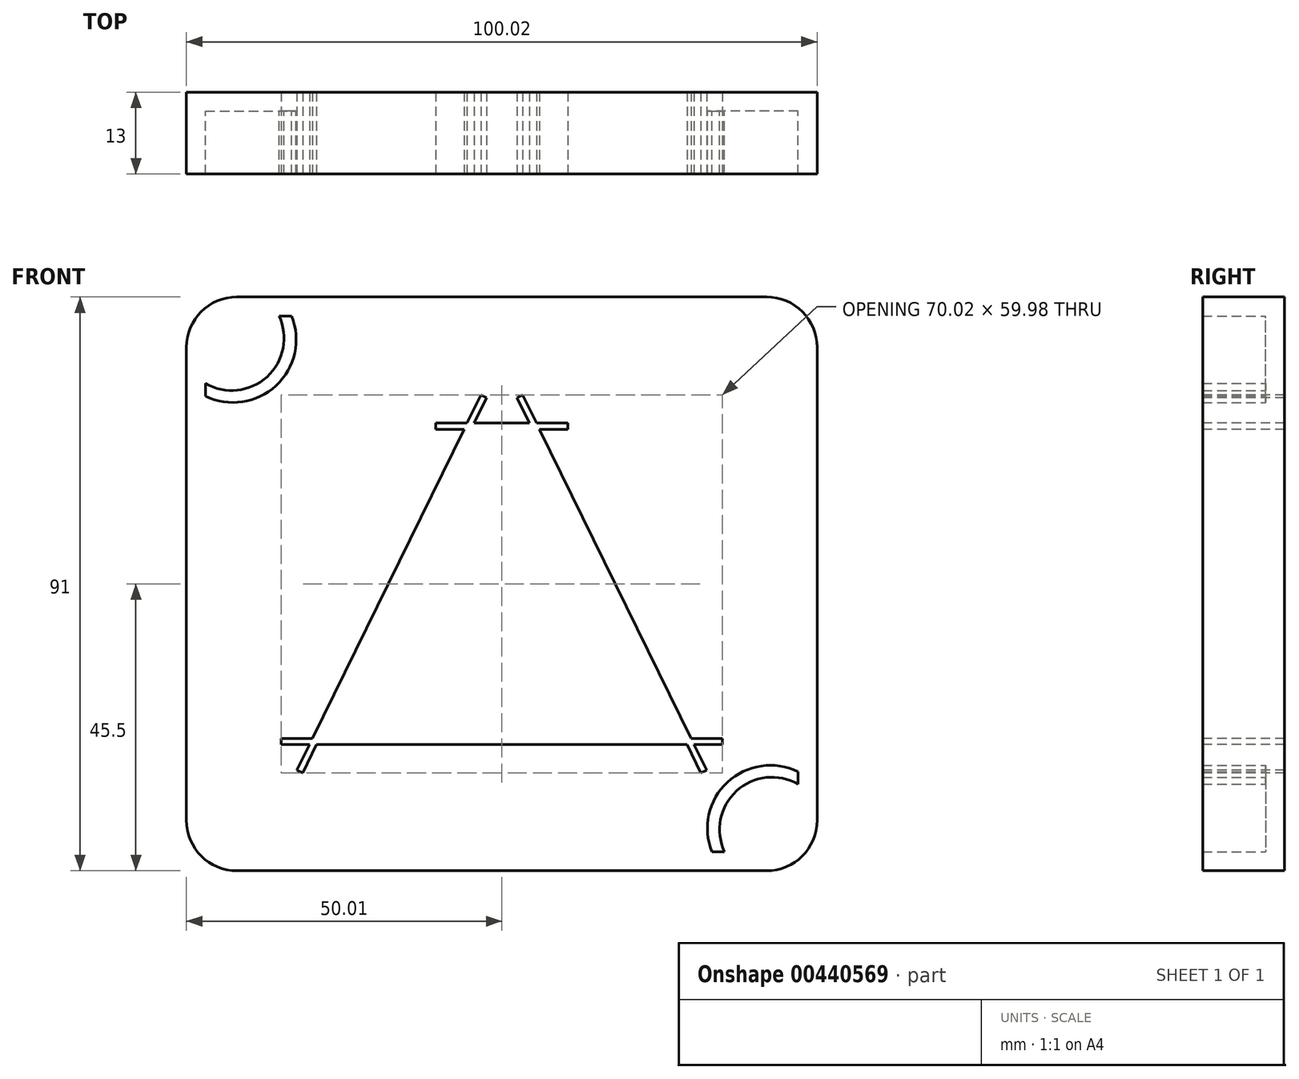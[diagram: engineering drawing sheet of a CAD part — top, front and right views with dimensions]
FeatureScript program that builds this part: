
annotation { "Feature Type Name" : "Feature", "Feature Type Description" : "" }
export const myFeature = defineFeature(function(context is Context, id is Id, definition is map)
    precondition{}
    {
        {
            var Q0;
            Q0=qCreatedBy(makeId("Front.planeOp"),FACE);
            var sketch = newSketch(context, id + "F0", { "sketchPlane" : qUnion([Q0])});
            skLineSegment(sketch, "E0", {"start": v(-29.39, 0) * mm, "end": v(0, 0) * mm});
            skLineSegment(sketch, "E1", {"start": v(0, 51) * mm, "end": v(-4.39, 51) * mm});
            skLineSegment(sketch, "E2", {"start": v(-6, 50) * mm, "end": v(-30, 1) * mm});
            skLineSegment(sketch, "E3", {"start": v(-31.61, 0) * mm, "end": v(-35, 0) * mm});
            skLineSegment(sketch, "E4", {"start": v(-35, 0) * mm, "end": v(-35, 1) * mm});
            skLineSegment(sketch, "E5", {"start": v(-35, 1) * mm, "end": v(-30, 1) * mm});
            skLineSegment(sketch, "E6", {"start": v(-5.5, 51) * mm, "end": v(-10.5, 51) * mm});
            skLineSegment(sketch, "E7", {"start": v(-5, 52) * mm, "end": v(-3.3, 55.49) * mm});
            skLineSegment(sketch, "E8.trimOffspring", {"start": v(-30.5, 0) * mm, "end": v(-32.49, -4.05) * mm});
            skPoint(sketch, "E9.end.orphan", {"position": v(-5.5, 55.49) * mm});
            skPoint(sketch, "E10.end.orphan", {"position": v(-7.96, 50.47) * mm});
            skPoint(sketch, "E11.trimOffspring.end.orphan", {"position": v(-5.5, 50.47) * mm});
            skLineSegment(sketch, "E12", {"start": v(-3.3, 55.49) * mm, "end": v(-2.4, 55.05) * mm});
            skLineSegment(sketch, "E13", {"start": v(-2.4, 55.05) * mm, "end": v(-4.39, 51) * mm});
            skPoint(sketch, "E14.end.orphan", {"position": v(6.46, 54.86) * mm});
            skPoint(sketch, "E15.end.orphan", {"position": v(5.5, 56.81) * mm});
            skPoint(sketch, "E16.end.orphan", {"position": v(13.73, 54.86) * mm});
            skLineSegment(sketch, "E17", {"start": v(-10.5, 51) * mm, "end": v(-10.5, 50) * mm});
            skLineSegment(sketch, "E18", {"start": v(-10.5, 50) * mm, "end": v(-6, 50) * mm});
            skLineSegment(sketch, "E19", {"start": v(-5, 52) * mm, "end": v(-5.5, 51) * mm});
            skLineSegment(sketch, "E20", {"start": v(-32.49, -4.05) * mm, "end": v(-31.59, -4.49) * mm});
            skLineSegment(sketch, "E21", {"start": v(-31.59, -4.49) * mm, "end": v(-29.39, 0) * mm});
            skLineSegment(sketch, "E22", {"start": v(-31.61, 0) * mm, "end": v(-30.5, 0) * mm});
            skLineSegment(sketch, "E23", {"start": v(0, 61.62) * mm, "end": v(0, -9.78) * mm, "construction": true});
            skPoint(sketch, "E24.start.orphan", {"position": v(5.5, 51) * mm});
            skLineSegment(sketch, "E25.MirrorCS", {"start": v(5, 52) * mm, "end": v(5.5, 51) * mm});
            skLineSegment(sketch, "E26.MirrorCS", {"start": v(31.61, 0) * mm, "end": v(30.5, 0) * mm});
            skLineSegment(sketch, "E27.MirrorCS", {"start": v(10.5, 51) * mm, "end": v(10.5, 50) * mm});
            skLineSegment(sketch, "E28.MirrorCS", {"start": v(31.61, 0) * mm, "end": v(35, 0) * mm});
            skLineSegment(sketch, "E29.MirrorCS", {"start": v(32.49, -4.05) * mm, "end": v(31.59, -4.49) * mm});
            skLineSegment(sketch, "E30.MirrorCS", {"start": v(2.4, 55.05) * mm, "end": v(4.39, 51) * mm});
            skLineSegment(sketch, "E31.MirrorCS", {"start": v(3.3, 55.49) * mm, "end": v(2.4, 55.05) * mm});
            skLineSegment(sketch, "E32.MirrorCS", {"start": v(30.5, 0) * mm, "end": v(32.49, -4.05) * mm});
            skLineSegment(sketch, "E33.MirrorCS", {"start": v(5, 52) * mm, "end": v(3.3, 55.49) * mm});
            skLineSegment(sketch, "E34.MirrorCS", {"start": v(35, 1) * mm, "end": v(30, 1) * mm});
            skLineSegment(sketch, "E35.MirrorCS", {"start": v(35, 0) * mm, "end": v(35, 1) * mm});
            skLineSegment(sketch, "E36.MirrorCS", {"start": v(10.5, 50) * mm, "end": v(6, 50) * mm});
            skLineSegment(sketch, "E37.MirrorCS", {"start": v(0, 51) * mm, "end": v(4.39, 51) * mm});
            skLineSegment(sketch, "E38.MirrorCS", {"start": v(31.59, -4.49) * mm, "end": v(29.39, 0) * mm});
            skLineSegment(sketch, "E39.MirrorCS", {"start": v(5.5, 51) * mm, "end": v(10.5, 51) * mm});
            skLineSegment(sketch, "E40.MirrorCS", {"start": v(6, 50) * mm, "end": v(30, 1) * mm});
            skPoint(sketch, "E41.MirrorP", {"position": v(5.5, 50.47) * mm});
            skPoint(sketch, "E42.MirrorP", {"position": v(5.5, 55.49) * mm});
            skPoint(sketch, "E43.MirrorP", {"position": v(7.96, 50.47) * mm});
            skLineSegment(sketch, "E44.MirrorCS", {"start": v(29.39, 0) * mm, "end": v(0, 0) * mm});
            skLineSegment(sketch, "E45.bottom", {"start": v(-50, 71) * mm, "end": v(50, 71) * mm});
            skLineSegment(sketch, "E45.top", {"start": v(-50, -20) * mm, "end": v(50, -20) * mm});
            skLineSegment(sketch, "E45.left", {"start": v(-50, 71) * mm, "end": v(-50, -20) * mm});
            skLineSegment(sketch, "E45.right", {"start": v(50, 71) * mm, "end": v(50, -20) * mm});
            skPoint(sketch, "E45.middle", {"position": v(0, 25.5) * mm});
            skSolve(sketch);
        }
        {
            var Q0;
            Q0=makeQuery(id+"F0.imprint","IMPRINT",FACE,{"disambiguationData":[TD([[makeQuery(id+"F0.imprint","IMPRINT",EDGE,{"derivedFrom":sQuery(id+"F0.wireOp",EDGE,"E0")}),-1.0]])]});
            var sketch = newSketch(context, id + "F1", { "sketchPlane" : qUnion([Q0])});
            skArc(sketch, "E46", {"start": v(33.33, 68) * mm, "mid": v(35.8, 56.95) * mm, "end": v(47, 55.29) * mm});
            skLineSegment(sketch, "E47", {"start": v(50, 71) * mm, "end": v(-50, -20) * mm, "construction": true});
            skLineSegment(sketch, "E48", {"start": v(-50, 71) * mm, "end": v(50, -20) * mm, "construction": true});
            skLineSegment(sketch, "E49", {"start": v(-50, 25.5) * mm, "end": v(50, 25.5) * mm, "construction": true});
            skArc(sketch, "E50.MirrorCS", {"start": v(33.33, -17) * mm, "mid": v(35.8, -5.95) * mm, "end": v(47, -4.29) * mm});
            skArc(sketch, "E51.MirrorCS", {"start": v(-33.33, 68) * mm, "mid": v(-35.8, 56.95) * mm, "end": v(-47, 55.29) * mm});
            skArc(sketch, "E52.MirrorCS", {"start": v(-33.33, -17) * mm, "mid": v(-35.8, -5.95) * mm, "end": v(-47, -4.29) * mm});
            skLineSegment(sketch, "E53", {"start": v(33.33, 68) * mm, "end": v(35.33, 68) * mm});
            skLineSegment(sketch, "E54", {"start": v(47, 55.29) * mm, "end": v(47, 57.29) * mm});
            skArc(sketch, "E55", {"start": v(35.33, 68) * mm, "mid": v(37.23, 58.35) * mm, "end": v(47, 57.29) * mm});
            skArc(sketch, "E56.MirrorCS", {"start": v(-35.33, 68) * mm, "mid": v(-37.23, 58.35) * mm, "end": v(-47, 57.29) * mm});
            skLineSegment(sketch, "E57.MirrorCS", {"start": v(-33.33, 68) * mm, "end": v(-35.33, 68) * mm});
            skLineSegment(sketch, "E58.MirrorCS", {"start": v(-47, 55.29) * mm, "end": v(-47, 57.29) * mm});
            skLineSegment(sketch, "E59.MirrorCS", {"start": v(47, -4.29) * mm, "end": v(47, -6.29) * mm});
            skArc(sketch, "E60.MirrorCS", {"start": v(35.33, -17) * mm, "mid": v(37.23, -7.35) * mm, "end": v(47, -6.29) * mm});
            skLineSegment(sketch, "E61.MirrorCS", {"start": v(33.33, -17) * mm, "end": v(35.33, -17) * mm});
            skArc(sketch, "E62.MirrorCS", {"start": v(-35.33, -17) * mm, "mid": v(-37.23, -7.35) * mm, "end": v(-47, -6.29) * mm});
            skLineSegment(sketch, "E63.MirrorCS", {"start": v(-47, -4.29) * mm, "end": v(-47, -6.29) * mm});
            skLineSegment(sketch, "E64.MirrorCS", {"start": v(-33.33, -17) * mm, "end": v(-35.33, -17) * mm});
            skSolve(sketch);
        }
        {
            var Q0;
            Q0 = qSketchRegion(id + "F0", true);
            extrude(context, id + "F2", {"entities" : qUnion([Q0]), "oppositeDirection" : true, "depth" : 3 * mm});
        }
        {
            var Q0;
            Q0=makeQuery(id+"F1.imprint","IMPRINT",FACE,{"disambiguationData":[TD([[makeQuery(id+"F1.imprint","IMPRINT",EDGE,{"derivedFrom":sQuery(id+"F1.wireOp",EDGE,"E52.MirrorCS")}),1.0]])]});
            var Q1;
            Q1=makeQuery(id+"F1.imprint","IMPRINT",FACE,{"disambiguationData":[TD([[makeQuery(id+"F1.imprint","IMPRINT",EDGE,{"derivedFrom":sQuery(id+"F1.wireOp",EDGE,"E51.MirrorCS")}),-1.0]])]});
            var Q2;
            Q2=makeQuery(id+"F1.imprint","IMPRINT",FACE,{"disambiguationData":[TD([[makeQuery(id+"F1.imprint","IMPRINT",EDGE,{"derivedFrom":sQuery(id+"F1.wireOp",EDGE,"E46")}),1.0]])]});
            var Q3;
            Q3=makeQuery(id+"F1.imprint","IMPRINT",FACE,{"disambiguationData":[TD([[makeQuery(id+"F1.imprint","IMPRINT",EDGE,{"derivedFrom":sQuery(id+"F1.wireOp",EDGE,"E50.MirrorCS")}),-1.0]])]});
            extrude(context, id + "F3", {"entities" : qUnion([Q0, Q1, Q2, Q3]), "operationType" : NewBodyOperationType.ADD, "depth" : 10 * mm});
        }
        {
            var Q0;
            Q0=makeQuery(id+"F2.opExtrude","SWEPT_EDGE",EDGE,{"disambiguationData":[OSD([sQuery(id+"F0.wireOp",EDGE,"E45.bottom"),sQuery(id+"F0.wireOp",EDGE,"E45.left")])]});
            var Q1;
            Q1=makeQuery(id+"F2.opExtrude","SWEPT_EDGE",EDGE,{"disambiguationData":[OSD([sQuery(id+"F0.wireOp",EDGE,"E45.bottom"),sQuery(id+"F0.wireOp",EDGE,"E45.right")])]});
            var Q2;
            Q2=makeQuery(id+"F2.opExtrude","SWEPT_EDGE",EDGE,{"disambiguationData":[OSD([sQuery(id+"F0.wireOp",EDGE,"E45.top"),sQuery(id+"F0.wireOp",EDGE,"E45.right")])]});
            var Q3;
            Q3=makeQuery(id+"F2.opExtrude","SWEPT_EDGE",EDGE,{"disambiguationData":[OSD([sQuery(id+"F0.wireOp",EDGE,"E45.top"),sQuery(id+"F0.wireOp",EDGE,"E45.left")])]});
            fillet(context, id + "F4", {"entities" : qUnion([Q0, Q1, Q2, Q3]), "radius" : 8 * mm, "tangentPropagation" : true, "allowEdgeOverflow" : false});
        }
    });
